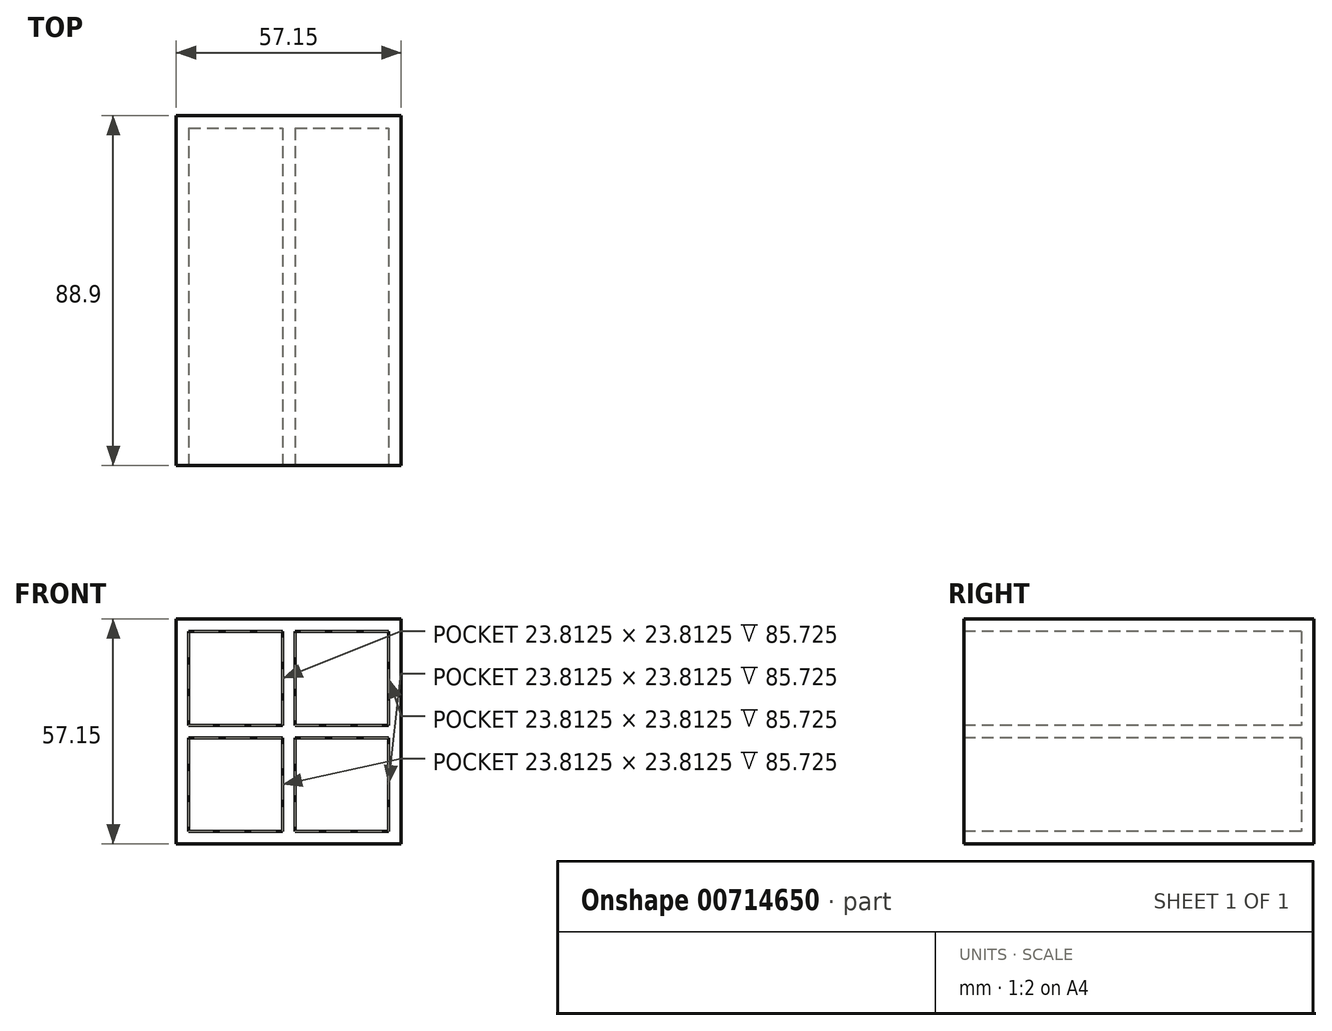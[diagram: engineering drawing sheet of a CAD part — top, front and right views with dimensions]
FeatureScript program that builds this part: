
annotation { "Feature Type Name" : "Feature", "Feature Type Description" : "" }
export const myFeature = defineFeature(function(context is Context, id is Id, definition is map)
    precondition{}
    {
        {
            var Q0;
            Q0=qCreatedBy(makeId("Front.planeOp"),FACE);
            var sketch = newSketch(context, id + "F0", { "sketchPlane" : qUnion([Q0])});
            skLineSegment(sketch, "E0.bottom", {"start": v(0, 0) * mm, "end": v(57.15, 0) * mm});
            skLineSegment(sketch, "E0.top", {"start": v(0, -57.15) * mm, "end": v(57.15, -57.15) * mm});
            skLineSegment(sketch, "E0.left", {"start": v(0, 0) * mm, "end": v(0, -57.15) * mm});
            skLineSegment(sketch, "E0.right", {"start": v(57.15, 0) * mm, "end": v(57.15, -57.15) * mm});
            skSolve(sketch);
        }
        {
            var Q0;
            Q0=makeQuery(id+"F0.imprint","IMPRINT",FACE,{"disambiguationData":[TD([[makeQuery(id+"F0.imprint","IMPRINT",EDGE,{"derivedFrom":sQuery(id+"F0.wireOp",EDGE,"E0.bottom")}),-1.0]])]});
            extrude(context, id + "F1", {"entities" : qUnion([Q0]), "depth" : 88.9 * mm, "offsetDistance" : 25.4 * mm});
        }
        {
            var Q0;
            Q0=makeQuery(id+"F1.opExtrude","CAP_FACE",FACE,{"disambiguationData":[OSD([sQuery(id+"F0.wireOp",EDGE,"E0.bottom"),sQuery(id+"F0.wireOp",EDGE,"E0.top"),sQuery(id+"F0.wireOp",EDGE,"E0.left"),sQuery(id+"F0.wireOp",EDGE,"E0.right")])],"isStart":false});
            var sketch = newSketch(context, id + "F2", { "sketchPlane" : qUnion([Q0])});
            skLineSegment(sketch, "E1", {"start": v(3.18, -26.99) * mm, "end": v(26.99, -26.99) * mm});
            skLineSegment(sketch, "E2", {"start": v(3.18, -30.16) * mm, "end": v(26.99, -30.16) * mm});
            skLineSegment(sketch, "E3", {"start": v(30.16, -3.18) * mm, "end": v(30.16, -26.99) * mm});
            skLineSegment(sketch, "E4", {"start": v(26.99, -3.18) * mm, "end": v(26.99, -26.99) * mm});
            skLineSegment(sketch, "E5", {"start": v(3.18, -3.18) * mm, "end": v(26.99, -3.18) * mm});
            skLineSegment(sketch, "E6", {"start": v(3.18, -3.18) * mm, "end": v(3.18, -26.99) * mm});
            skLineSegment(sketch, "E7", {"start": v(53.98, -3.18) * mm, "end": v(53.98, -26.99) * mm});
            skLineSegment(sketch, "E8", {"start": v(3.18, -53.98) * mm, "end": v(26.99, -53.98) * mm});
            skLineSegment(sketch, "E9.trimOffspring", {"start": v(30.16, -3.18) * mm, "end": v(53.98, -3.18) * mm});
            skPoint(sketch, "E10.orphan", {"position": v(57.15, -3.18) * mm});
            skLineSegment(sketch, "E11.trimOffspring", {"start": v(30.16, -26.99) * mm, "end": v(53.98, -26.99) * mm});
            skLineSegment(sketch, "E12.trimOffspring", {"start": v(30.16, -30.16) * mm, "end": v(30.16, -53.98) * mm});
            skLineSegment(sketch, "E13.trimOffspring", {"start": v(30.16, -30.16) * mm, "end": v(53.98, -30.16) * mm});
            skLineSegment(sketch, "E14.trimOffspring", {"start": v(26.99, -30.16) * mm, "end": v(26.99, -53.98) * mm});
            skPoint(sketch, "E15.orphan", {"position": v(57.15, -53.98) * mm});
            skLineSegment(sketch, "E16.trimOffspring", {"start": v(30.16, -53.98) * mm, "end": v(53.98, -53.98) * mm});
            skLineSegment(sketch, "E17.trimOffspring", {"start": v(3.18, -30.16) * mm, "end": v(3.18, -53.98) * mm});
            skLineSegment(sketch, "E18.trimOffspring", {"start": v(53.98, -30.16) * mm, "end": v(53.98, -53.98) * mm});
            skPoint(sketch, "E19.orphan", {"position": v(3.18, -57.15) * mm});
            skSolve(sketch);
        }
        {
            var Q0;
            Q0 = qSketchRegion(id + "F2", true);
            extrude(context, id + "F3", {"entities" : qUnion([Q0]), "operationType" : NewBodyOperationType.REMOVE, "oppositeDirection" : true, "depth" : 85.72 * mm, "offsetDistance" : 25.4 * mm});
        }
    });
